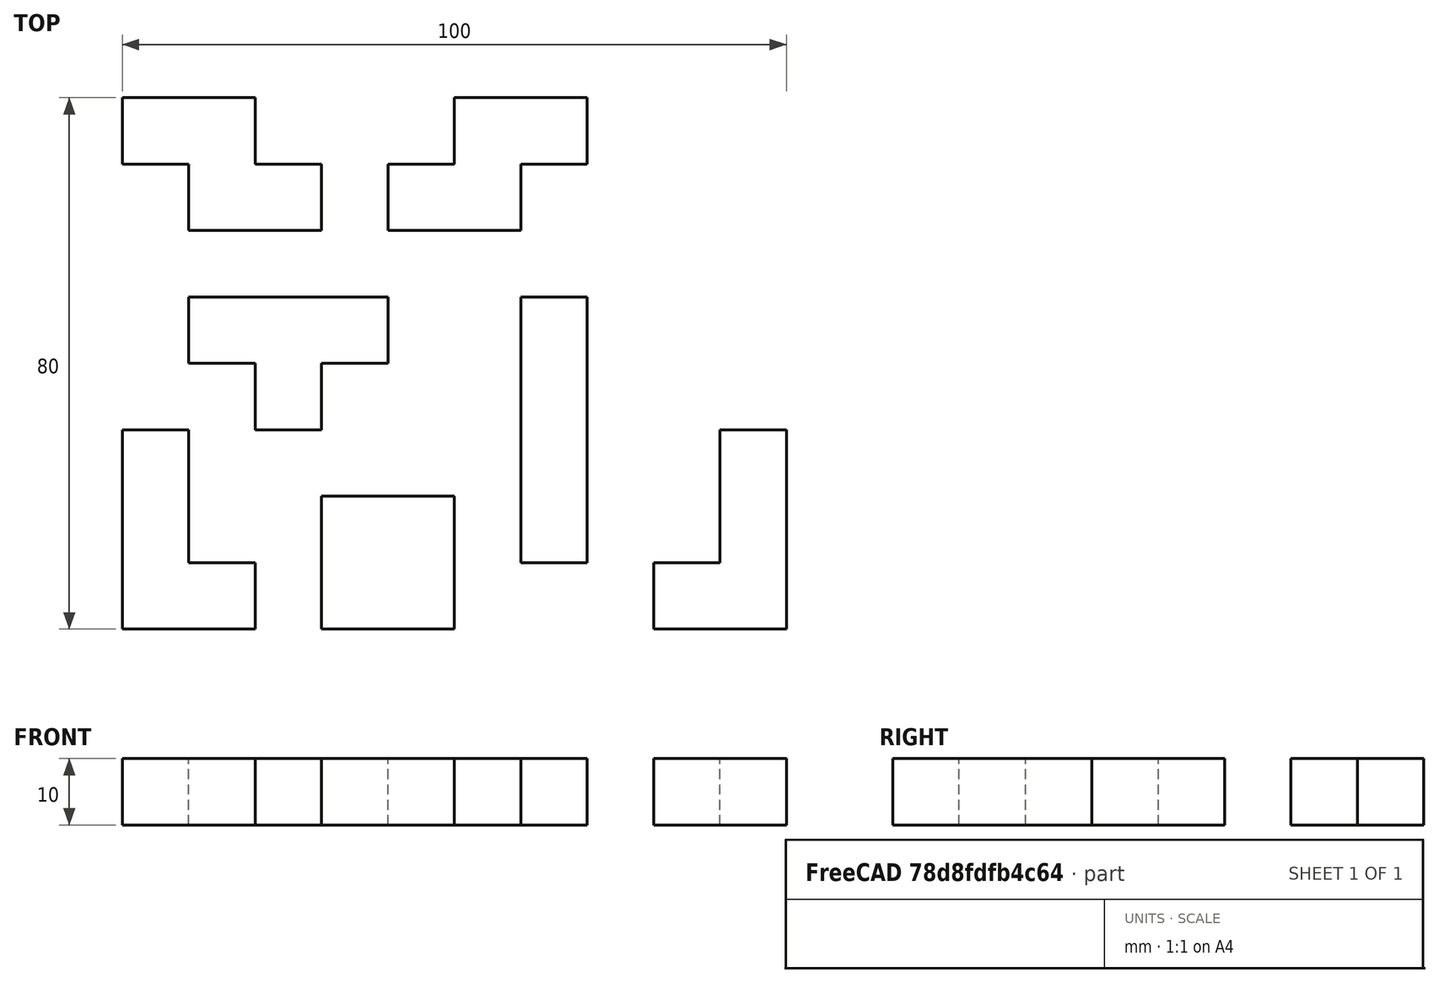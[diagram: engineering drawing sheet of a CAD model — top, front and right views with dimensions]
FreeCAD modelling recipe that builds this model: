
FCSTD DOCUMENT  (FreeCAD 1.0R39319 (Git))
Label: ojt1_t05r03_tetris
License: All rights reserved
LicenseURL: https://en.wikipedia.org/wiki/All_rights_reserved
objects: Part::Box×32, Part::MultiFuse×8
note: 40 computed .brp shape members not serialized (recipe doc carries the construction recipe); baked Part::Feature solids carry a one-line shape summary decoded from their .brp

FEATURE [Part::Box] Box  label="Cube"
  AttacherType = Attacher::AttachEngine3D
  Height = 10
  Length = 10
  Width = 10
FEATURE [Part::Box] Box001  label="Cube001"
  AttacherType = Attacher::AttachEngine3D
  Height = 10
  Length = 10
  Placement = pos=(0,-10,0) rot=(0,0,1;0rad)
  Width = 10
FEATURE [Part::Box] Box002  label="Cube002"
  AttacherType = Attacher::AttachEngine3D
  Height = 10
  Length = 10
  Placement = pos=(0,-20,0) rot=(0,0,1;0rad)
  Width = 10
FEATURE [Part::Box] Box003  label="Cube003"
  AttacherType = Attacher::AttachEngine3D
  Height = 10
  Length = 10
  Placement = pos=(0,-30,0) rot=(0,0,1;0rad)
  Width = 10
FEATURE [Part::MultiFuse] Fusion
  Refine = true
  Shapes = -> [Box,Box001,Box002,Box003]
FEATURE [Part::Box] Box004  label="Cube004"
  AttacherType = Attacher::AttachEngine3D
  Height = 10
  Length = 10
  Placement = pos=(-30,0,0) rot=(0,0,1;0rad)
  Width = 10
FEATURE [Part::Box] Box005  label="Cube005"
  AttacherType = Attacher::AttachEngine3D
  Height = 10
  Length = 10
  Placement = pos=(-40,0,0) rot=(0,0,1;0rad)
  Width = 10
FEATURE [Part::Box] Box006  label="Cube006"
  AttacherType = Attacher::AttachEngine3D
  Height = 10
  Length = 10
  Placement = pos=(-50,0,0) rot=(0,0,1;0rad)
  Width = 10
FEATURE [Part::Box] Box007  label="Cube007"
  AttacherType = Attacher::AttachEngine3D
  Height = 10
  Length = 10
  Placement = pos=(-40,-10,0) rot=(0,0,1;0rad)
  Width = 10
FEATURE [Part::MultiFuse] Fusion001
  Refine = true
  Shapes = -> [Box004,Box005,Box006,Box007]
FEATURE [Part::Box] Box008  label="Cube008"
  AttacherType = Attacher::AttachEngine3D
  Height = 10
  Length = 10
  Placement = pos=(-20,-30,0) rot=(0,0,1;0rad)
  Width = 10
FEATURE [Part::Box] Box009  label="Cube009"
  AttacherType = Attacher::AttachEngine3D
  Height = 10
  Length = 10
  Placement = pos=(-30,-30,0) rot=(0,0,1;0rad)
  Width = 10
FEATURE [Part::Box] Box010  label="Cube010"
  AttacherType = Attacher::AttachEngine3D
  Height = 10
  Length = 10
  Placement = pos=(-30,-40,0) rot=(0,0,1;0rad)
  Width = 10
FEATURE [Part::Box] Box011  label="Cube011"
  AttacherType = Attacher::AttachEngine3D
  Height = 10
  Length = 10
  Placement = pos=(-20,-40,0) rot=(0,0,1;0rad)
  Width = 10
FEATURE [Part::MultiFuse] Fusion002
  Refine = true
  Shapes = -> [Box008,Box009,Box010,Box011]
FEATURE [Part::Box] Box012  label="Cube012"
  AttacherType = Attacher::AttachEngine3D
  Height = 10
  Length = 10
  Placement = pos=(-60,-40,0) rot=(0,0,1;0rad)
  Width = 10
FEATURE [Part::Box] Box013  label="Cube013"
  AttacherType = Attacher::AttachEngine3D
  Height = 10
  Length = 10
  Placement = pos=(-60,-30,0) rot=(0,0,1;0rad)
  Width = 10
FEATURE [Part::Box] Box014  label="Cube014"
  AttacherType = Attacher::AttachEngine3D
  Height = 10
  Length = 10
  Placement = pos=(-60,-20,0) rot=(0,0,1;0rad)
  Width = 10
FEATURE [Part::Box] Box015  label="Cube015"
  AttacherType = Attacher::AttachEngine3D
  Height = 10
  Length = 10
  Placement = pos=(-50,-40,0) rot=(0,0,1;0rad)
  Width = 10
FEATURE [Part::MultiFuse] Fusion003
  Refine = true
  Shapes = -> [Box012,Box013,Box014,Box015]
FEATURE [Part::Box] Box016  label="Cube016"
  AttacherType = Attacher::AttachEngine3D
  Height = 10
  Length = 10
  Placement = pos=(-60,-40,0) rot=(0,0,1;0rad)
  Width = 10
FEATURE [Part::Box] Box017  label="Cube017"
  AttacherType = Attacher::AttachEngine3D
  Height = 10
  Length = 10
  Placement = pos=(-60,-30,0) rot=(0,0,1;0rad)
  Width = 10
FEATURE [Part::Box] Box018  label="Cube018"
  AttacherType = Attacher::AttachEngine3D
  Height = 10
  Length = 10
  Placement = pos=(-60,-20,0) rot=(0,0,1;0rad)
  Width = 10
FEATURE [Part::Box] Box019  label="Cube019"
  AttacherType = Attacher::AttachEngine3D
  Height = 10
  Length = 10
  Placement = pos=(-50,-40,0) rot=(0,0,1;0rad)
  Width = 10
FEATURE [Part::MultiFuse] Fusion004
  Refine = true
  Shapes = -> [Box016,Box017,Box018,Box019]
FEATURE [Part::Box] Box020  label="Cube020"
  AttacherType = Attacher::AttachEngine3D
  Height = 10
  Length = 10
  Placement = pos=(30,-40,0) rot=(0,0,1;0rad)
  Width = 10
FEATURE [Part::Box] Box021  label="Cube021"
  AttacherType = Attacher::AttachEngine3D
  Height = 10
  Length = 10
  Placement = pos=(30,-30,0) rot=(0,0,1;0rad)
  Width = 10
FEATURE [Part::Box] Box022  label="Cube022"
  AttacherType = Attacher::AttachEngine3D
  Height = 10
  Length = 10
  Placement = pos=(30,-20,0) rot=(0,0,1;0rad)
  Width = 10
FEATURE [Part::Box] Box023  label="Cube023"
  AttacherType = Attacher::AttachEngine3D
  Height = 10
  Length = 10
  Placement = pos=(20,-40,0) rot=(0,0,1;0rad)
  Width = 10
FEATURE [Part::MultiFuse] Fusion005
  Refine = true
  Shapes = -> [Box020,Box021,Box022,Box023]
FEATURE [Part::Box] Box024  label="Cube024"
  AttacherType = Attacher::AttachEngine3D
  Height = 10
  Length = 10
  Placement = pos=(-20,20,0) rot=(0,0,1;0rad)
  Width = 10
FEATURE [Part::Box] Box025  label="Cube025"
  AttacherType = Attacher::AttachEngine3D
  Height = 10
  Length = 10
  Placement = pos=(-10,20,0) rot=(0,0,1;0rad)
  Width = 10
FEATURE [Part::Box] Box026  label="Cube026"
  AttacherType = Attacher::AttachEngine3D
  Height = 10
  Length = 10
  Placement = pos=(-10,30,0) rot=(0,0,1;0rad)
  Width = 10
FEATURE [Part::Box] Box027  label="Cube027"
  AttacherType = Attacher::AttachEngine3D
  Height = 10
  Length = 10
  Placement = pos=(0,30,0) rot=(0,0,1;0rad)
  Width = 10
FEATURE [Part::MultiFuse] Fusion006
  Refine = true
  Shapes = -> [Box024,Box025,Box026,Box027]
FEATURE [Part::Box] Box028  label="Cube028"
  AttacherType = Attacher::AttachEngine3D
  Height = 10
  Length = 10
  Placement = pos=(-60,30,0) rot=(0,0,1;0rad)
  Width = 10
FEATURE [Part::Box] Box029  label="Cube029"
  AttacherType = Attacher::AttachEngine3D
  Height = 10
  Length = 10
  Placement = pos=(-50,30,0) rot=(0,0,1;0rad)
  Width = 10
FEATURE [Part::Box] Box030  label="Cube030"
  AttacherType = Attacher::AttachEngine3D
  Height = 10
  Length = 10
  Placement = pos=(-50,20,0) rot=(0,0,1;0rad)
  Width = 10
FEATURE [Part::Box] Box031  label="Cube031"
  AttacherType = Attacher::AttachEngine3D
  Height = 10
  Length = 10
  Placement = pos=(-40,20,0) rot=(0,0,1;0rad)
  Width = 10
FEATURE [Part::MultiFuse] Fusion007
  Refine = true
  Shapes = -> [Box028,Box029,Box030,Box031]
